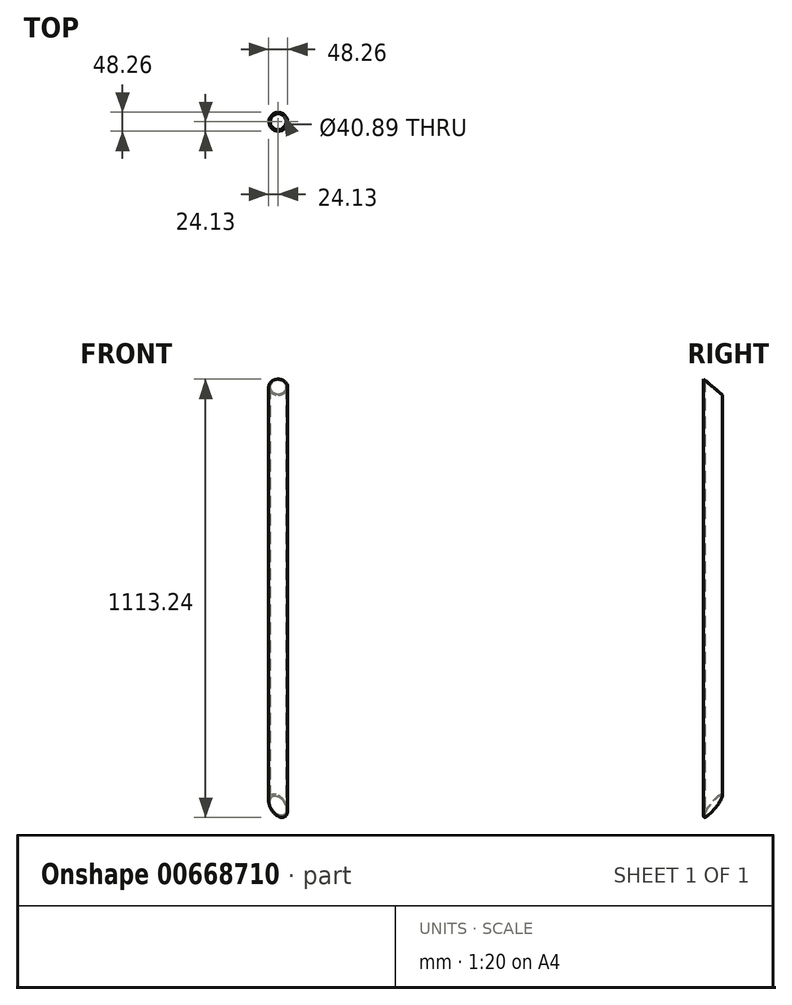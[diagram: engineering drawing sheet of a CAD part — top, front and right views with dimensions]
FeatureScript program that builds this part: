
annotation { "Feature Type Name" : "Feature", "Feature Type Description" : "" }
export const myFeature = defineFeature(function(context is Context, id is Id, definition is map)
    precondition{}
    {
        {
            var Q0;
            Q0=qCreatedBy(makeId("Top.planeOp"),FACE);
            var sketch = newSketch(context, id + "F0", { "sketchPlane" : qUnion([Q0])});
            skCircle(sketch, "E0", {"center": v(0, 0) * mm, "radius": 20.45 * mm});
            skCircle(sketch, "E1.0", {"center": v(0, 0) * mm, "radius": 24.13 * mm});
            skSolve(sketch);
        }
        {
            var Q0;
            Q0=qSketchRegion(id+"F0",true);
            extrude(context, id + "F1", {"entities" : qUnion([Q0]), "depth" : 1130.3 * mm, "offsetDistance" : 25.4 * mm});
        }
        {
            var Q0;
            Q0=qCreatedBy(makeId("Right.planeOp"),FACE);
            var sketch = newSketch(context, id + "F2", { "sketchPlane" : qUnion([Q0])});
            skLineSegment(sketch, "E2.bottom", {"start": v(24.13, 1130.3) * mm, "end": v(-24.13, 1130.3) * mm});
            skLineSegment(sketch, "E2.left", {"start": v(24.13, 1130.3) * mm, "end": v(24.13, 1089.8) * mm});
            skPoint(sketch, "E2.middle", {"position": v(0, 1110.05) * mm});
            skLineSegment(sketch, "E3", {"start": v(-24.13, 1130.3) * mm, "end": v(24.13, 1089.8) * mm});
            skPoint(sketch, "E2.top.end.orphan", {"position": v(-24.13, 1089.8) * mm});
            skSolve(sketch);
        }
        {
            var Q0;
            Q0=qSketchRegion(id+"F2",true);
            extrude(context, id + "F3", {"entities" : qUnion([Q0]), "operationType" : NewBodyOperationType.REMOVE, "endBound" : BoundingType.THROUGH_ALL, "oppositeDirection" : true, "depth" : 25.4 * mm, "hasSecondDirection" : true, "secondDirectionBound" : SecondDirectionBoundingType.THROUGH_ALL, "secondDirectionOppositeDirection" : false, "secondDirectionDepth" : 25.4 * mm});
        }
        {
            var Q0;
            Q0=qCreatedBy(makeId("Front.planeOp"),FACE);
            var sketch = newSketch(context, id + "F4", { "sketchPlane" : qUnion([Q0])});
            skLineSegment(sketch, "E4.top", {"start": v(28.58, 0) * mm, "end": v(-28.58, 0) * mm});
            skPoint(sketch, "E4.middle", {"position": v(0, 14.55) * mm});
            skPoint(sketch, "E4.right.start.orphan", {"position": v(-28.58, 29.1) * mm});
            skLineSegment(sketch, "E5", {"start": v(-28.58, 29.1) * mm, "end": v(-28.58, 0) * mm});
            skLineSegment(sketch, "E6", {"start": v(-28.57, 29.1) * mm, "end": v(28.57, 0) * mm});
            skPoint(sketch, "E4.left.start.orphan", {"position": v(28.58, 29.1) * mm});
            skSolve(sketch);
        }
        {
            var Q0;
            Q0=qSketchRegion(id+"F4",true);
            extrude(context, id + "F5", {"entities" : qUnion([Q0]), "operationType" : NewBodyOperationType.REMOVE, "endBound" : BoundingType.THROUGH_ALL, "depth" : 25.4 * mm, "hasSecondDirection" : true, "secondDirectionBound" : SecondDirectionBoundingType.THROUGH_ALL, "secondDirectionOppositeDirection" : true, "secondDirectionDepth" : 25.4 * mm});
        }
        {
            var Q0;
            Q0=makeQuery(id+"F5.boolean.opBoolean","COPY",FACE,{"derivedFrom":makeQuery(id+"F5.opExtrude","SWEPT_FACE",FACE,{"disambiguationData":[OSD([sQuery(id+"F4.wireOp",EDGE,"E6")])]})});
            var sketch = newSketch(context, id + "F6", { "sketchPlane" : qUnion([Q0])});
            skLineSegment(sketch, "E7", {"start": v(-29.55, 0) * mm, "end": v(16.34, 0) * mm});
            skSolve(sketch);
        }
        {
            var Q0;
            Q0=sQuery(id+"F6.wireOp",EDGE,"E7");
            cPlane(context, id + "F7", {"entities" : qUnion([Q0]), "cplaneType" : CPlaneType.LINE_ANGLE, "offset" : 25.4 * mm, "angle" : 45 * degree, "oppositeDirection" : true, "width" : 152.4 * mm, "height" : 152.4 * mm});
        }
        {
            var Q0;
            Q0=qCreatedBy(id+"F7.planeOp",FACE);
            var sketch = newSketch(context, id + "F8", { "sketchPlane" : qUnion([Q0])});
            skLineSegment(sketch, "E8.bottom", {"start": v(-83.87, 91.05) * mm, "end": v(94.55, 91.05) * mm});
            skLineSegment(sketch, "E8.top", {"start": v(-83.87, -76.34) * mm, "end": v(94.55, -76.34) * mm});
            skLineSegment(sketch, "E8.left", {"start": v(-83.87, 91.05) * mm, "end": v(-83.87, -76.34) * mm});
            skLineSegment(sketch, "E8.right", {"start": v(94.55, 91.05) * mm, "end": v(94.55, -76.34) * mm});
            skPoint(sketch, "E8.middle", {"position": v(5.34, 7.36) * mm});
            skSolve(sketch);
        }
        {
            var Q0;
            Q0=qSketchRegion(id+"F8",true);
            extrude(context, id + "F9", {"entities" : qUnion([Q0]), "operationType" : NewBodyOperationType.REMOVE, "depth" : 50.8 * mm, "hasSecondDirection" : true, "secondDirectionOppositeDirection" : true, "secondDirectionDepth" : 20.32 * mm});
        }
    });
